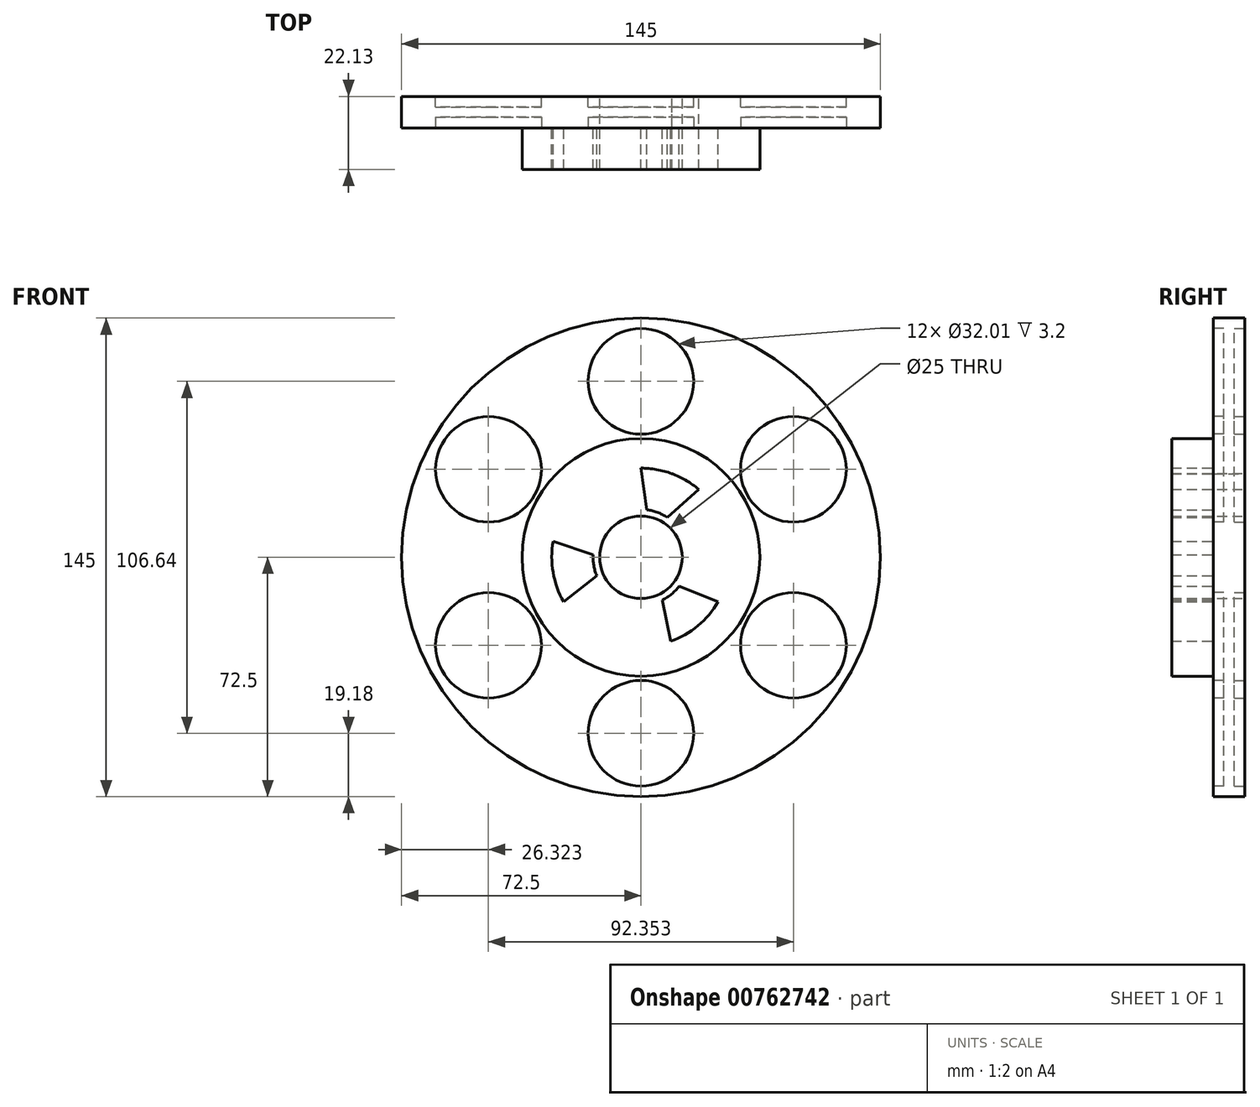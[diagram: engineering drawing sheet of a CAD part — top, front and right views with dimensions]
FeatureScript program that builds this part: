
annotation { "Feature Type Name" : "Feature", "Feature Type Description" : "" }
export const myFeature = defineFeature(function(context is Context, id is Id, definition is map)
    precondition{}
    {
        {
            var Q0;
            Q0=qCreatedBy(makeId("Front.planeOp"),FACE);
            var sketch = newSketch(context, id + "F0", { "sketchPlane" : qUnion([Q0])});
            skCircle(sketch, "E0", {"center": v(0, 0) * mm, "radius": 72.5 * mm});
            skCircle(sketch, "E1", {"center": v(0, 0) * mm, "radius": 12.5 * mm});
            skPoint(sketch, "E2", {"position": v(0, 27) * mm});
            skCircle(sketch, "E3", {"center": v(0, 0) * mm, "radius": 36 * mm});
            skLineSegment(sketch, "E4", {"start": v(0, -72.5) * mm, "end": v(0, -53.32) * mm});
            skCircle(sketch, "E5", {"center": v(0, 0) * mm, "radius": 27.02 * mm});
            skLineSegment(sketch, "E6", {"start": v(0, 0) * mm, "end": v(0, 27) * mm});
            skLineSegment(sketch, "E7", {"start": v(0, 0) * mm, "end": v(17.53, 20.56) * mm});
            skLineSegment(sketch, "E8", {"start": v(0, 0) * mm, "end": v(9.34, 25.35) * mm});
            skArc(sketch, "E9", {"start": v(0, 27) * mm, "mid": v(9.33, 25.34) * mm, "end": v(17.52, 20.55) * mm});
            skLineSegment(sketch, "E10", {"start": v(0, 0) * mm, "end": v(7.95, 12.12) * mm});
            skLineSegment(sketch, "E11", {"start": v(0, 0) * mm, "end": v(1.81, 14.39) * mm});
            skArc(sketch, "E12", {"start": v(1.81, 14.39) * mm, "mid": v(5.01, 13.6) * mm, "end": v(7.95, 12.12) * mm});
            skLineSegment(sketch, "E13", {"start": v(1.81, 14.39) * mm, "end": v(0, 27) * mm});
            skLineSegment(sketch, "E14", {"start": v(7.95, 12.12) * mm, "end": v(17.53, 20.56) * mm});
            skLineSegment(sketch, "E15.1.0", {"start": v(-13.37, -5.62) * mm, "end": v(-23.38, -13.5) * mm});
            skArc(sketch, "E15.1.1", {"start": v(-23.38, -13.5) * mm, "mid": v(-26.6, -4.58) * mm, "end": v(-26.55, 4.9) * mm});
            skLineSegment(sketch, "E15.1.2", {"start": v(-14.48, 0.83) * mm, "end": v(-26.57, 4.9) * mm});
            skArc(sketch, "E15.1.3", {"start": v(-13.37, -5.62) * mm, "mid": v(-14.29, -2.46) * mm, "end": v(-14.48, 0.83) * mm});
            skLineSegment(sketch, "E15.2.0", {"start": v(11.55, -8.76) * mm, "end": v(23.38, -13.5) * mm});
            skArc(sketch, "E15.2.1", {"start": v(23.38, -13.5) * mm, "mid": v(17.27, -20.75) * mm, "end": v(9.04, -25.44) * mm});
            skLineSegment(sketch, "E15.2.2", {"start": v(6.52, -12.95) * mm, "end": v(9.04, -25.46) * mm});
            skArc(sketch, "E15.2.3", {"start": v(11.55, -8.76) * mm, "mid": v(9.28, -11.14) * mm, "end": v(6.52, -12.95) * mm});
            skSolve(sketch);
        }
        {
            var Q0;
            Q0=makeQuery(id+"F0.imprint","IMPRINT",FACE,{"disambiguationData":[TD([[makeQuery(id+"F0.imprint","IMPRINT",EDGE,{"derivedFrom":sQuery(id+"F0.wireOp",EDGE,"E3")}),1.0]])]});
            var Q1;
            {var subQ16=sQuery(id+"F0.wireOp",EDGE,"E15.1.0");Q1=makeQuery(id+"F0.imprint","IMPRINT",FACE,{"disambiguationData":[TD([[makeQuery(id+"F0.imprint","IMPRINT",EDGE,{"derivedFrom":subQ16}),1.0]])]});}
            var Q2;
            {var subQ5=sQuery(id+"F0.wireOp",EDGE,"E10");var subQ7=sQuery(id+"F0.wireOp",EDGE,"E1");var subQ8=makeQuery(id+"F0.imprint","INTERSECT",VERTEX,{"derivedFrom":[subQ7,subQ5]});Q2=makeQuery(id+"F0.imprint","IMPRINT",FACE,{"disambiguationData":[TD([[makeQuery(id+"F0.imprint","IMPRINT",EDGE,{"disambiguationData":[TD([[subQ8,1.0]])],"derivedFrom":subQ7}),-1.0]])]});}
            var Q3;
            {var subQ0=sQuery(id+"F0.wireOp",EDGE,"E10");var subQ1=sQuery(id+"F0.wireOp",EDGE,"E1");var subQ2=makeQuery(id+"F0.imprint","INTERSECT",VERTEX,{"derivedFrom":[subQ1,subQ0]});Q3=makeQuery(id+"F0.imprint","IMPRINT",FACE,{"disambiguationData":[TD([[makeQuery(id+"F0.imprint","IMPRINT",EDGE,{"disambiguationData":[TD([[subQ2,-1.0]])],"derivedFrom":subQ1}),-1.0]])]});}
            var Q4;
            {var subQ0=sQuery(id+"F0.wireOp",EDGE,"E8");var subQ1=sQuery(id+"F0.wireOp",EDGE,"E1");var subQ2=makeQuery(id+"F0.imprint","INTERSECT",VERTEX,{"derivedFrom":[subQ1,subQ0]});Q4=makeQuery(id+"F0.imprint","IMPRINT",FACE,{"disambiguationData":[TD([[makeQuery(id+"F0.imprint","IMPRINT",EDGE,{"disambiguationData":[TD([[subQ2,-1.0]])],"derivedFrom":subQ1}),-1.0]])]});}
            var Q5;
            {var subQ5=sQuery(id+"F0.wireOp",EDGE,"E13");Q5=makeQuery(id+"F0.imprint","IMPRINT",FACE,{"disambiguationData":[TD([[makeQuery(id+"F0.imprint","IMPRINT",EDGE,{"derivedFrom":subQ5}),1.0]])]});}
            extrude(context, id + "F1", {"entities" : qUnion([Q0, Q1, Q2, Q3, Q4, Q5]), "depth" : 22.12 * mm, "offsetDistance" : 25.4 * mm});
        }
        {
            var Q0;
            Q0=makeQuery(id+"F0.imprint","IMPRINT",FACE,{"disambiguationData":[TD([[makeQuery(id+"F0.imprint","IMPRINT",EDGE,{"derivedFrom":sQuery(id+"F0.wireOp",EDGE,"E0")}),1.0]])]});
            var Q1;
            {var subQ5=sQuery(id+"F0.wireOp",EDGE,"E13");Q1=makeQuery(id+"F0.imprint","IMPRINT",FACE,{"disambiguationData":[TD([[makeQuery(id+"F0.imprint","IMPRINT",EDGE,{"derivedFrom":subQ5}),-1.0]])]});}
            var Q2;
            {var subQ0=sQuery(id+"F0.wireOp",EDGE,"E12");var subQ1=sQuery(id+"F0.wireOp",EDGE,"E8");var subQ2=makeQuery(id+"F0.imprint","INTERSECT",VERTEX,{"derivedFrom":[subQ1,subQ0]});Q2=makeQuery(id+"F0.imprint","IMPRINT",FACE,{"disambiguationData":[TD([[makeQuery(id+"F0.imprint","IMPRINT",EDGE,{"disambiguationData":[TD([[subQ2,-1.0]])],"derivedFrom":subQ1}),-1.0]])]});}
            var Q3;
            {var subQ0=sQuery(id+"F0.wireOp",EDGE,"E15.2.0");Q3=makeQuery(id+"F0.imprint","IMPRINT",FACE,{"disambiguationData":[TD([[makeQuery(id+"F0.imprint","IMPRINT",EDGE,{"derivedFrom":subQ0}),-1.0]])]});}
            var Q4;
            {var subQ0=sQuery(id+"F0.wireOp",EDGE,"E15.1.0");Q4=makeQuery(id+"F0.imprint","IMPRINT",FACE,{"disambiguationData":[TD([[makeQuery(id+"F0.imprint","IMPRINT",EDGE,{"derivedFrom":subQ0}),-1.0]])]});}
            extrude(context, id + "F2", {"entities" : qUnion([Q0, Q1, Q2, Q3, Q4]), "operationType" : NewBodyOperationType.ADD, "depth" : 9.53 * mm, "offsetDistance" : 25 * mm});
        }
        {
            var Q0;
            Q0=makeQuery(id+"F0.imprint","IMPRINT",FACE,{"disambiguationData":[TD([[makeQuery(id+"F0.imprint","IMPRINT",EDGE,{"derivedFrom":sQuery(id+"F0.wireOp",EDGE,"E0")}),1.0]])]});
            var sketch = newSketch(context, id + "F3", { "sketchPlane" : qUnion([Q0])});
            skCircle(sketch, "E16", {"center": v(0, -53.32) * mm, "radius": 16 * mm});
            skCircle(sketch, "E17.1.0", {"center": v(46.18, -26.66) * mm, "radius": 16 * mm});
            skCircle(sketch, "E17.2.0", {"center": v(46.18, 26.66) * mm, "radius": 16 * mm});
            skCircle(sketch, "E17.3.0", {"center": v(0, 53.32) * mm, "radius": 16 * mm});
            skCircle(sketch, "E17.4.0", {"center": v(-46.18, 26.66) * mm, "radius": 16 * mm});
            skCircle(sketch, "E17.5.0", {"center": v(-46.18, -26.66) * mm, "radius": 16 * mm});
            skPoint(sketch, "E17.center", {"position": v(0, 0) * mm});
            skSolve(sketch);
        }
        {
            var Q0;
            Q0 = qSketchRegion(id + "F3", true);
            extrude(context, id + "F4", {"entities" : qUnion([Q0]), "operationType" : NewBodyOperationType.REMOVE, "depth" : 3.2 * mm, "offsetDistance" : 25 * mm});
        }
        {
            var Q0;
            Q0=makeQuery(id+"F2.opExtrude","CAP_FACE",FACE,{"disambiguationData":[OSD([sQuery(id+"F0.wireOp",EDGE,"E0"),sQuery(id+"F0.wireOp",EDGE,"E3")])],"isStart":false});
            var sketch = newSketch(context, id + "F5", { "sketchPlane" : qUnion([Q0])});
            skCircle(sketch, "E18", {"center": v(0, -53.32) * mm, "radius": 16 * mm});
            skCircle(sketch, "E19.1.0", {"center": v(46.18, -26.66) * mm, "radius": 16 * mm});
            skCircle(sketch, "E19.2.0", {"center": v(46.18, 26.66) * mm, "radius": 16 * mm});
            skCircle(sketch, "E19.3.0", {"center": v(0, 53.32) * mm, "radius": 16 * mm});
            skCircle(sketch, "E19.4.0", {"center": v(-46.18, 26.66) * mm, "radius": 16 * mm});
            skCircle(sketch, "E19.5.0", {"center": v(-46.18, -26.66) * mm, "radius": 16 * mm});
            skPoint(sketch, "E19.center", {"position": v(0, 0) * mm});
            skSolve(sketch);
        }
        {
            var Q0;
            Q0 = qSketchRegion(id + "F5", true);
            extrude(context, id + "F6", {"entities" : qUnion([Q0]), "operationType" : NewBodyOperationType.REMOVE, "oppositeDirection" : true, "depth" : 3.2 * mm, "offsetDistance" : 25 * mm});
        }
    });
